FCSTD DOCUMENT  (FreeCAD 0.17R13541 (Git))
Label: L_Wuerth_WE-TPC-3816
License: All rights reserved
LicenseURL: http://en.wikipedia.org/wiki/All_rights_reserved
objects: Sketcher::SketchObject×5, App::Annotation×2, App::DocumentObjectGroup×1
note: 5 computed .brp shape members not serialized (recipe doc carries the construction recipe); baked Part::Feature solids carry a one-line shape summary decoded from their .brp

FEATURE [Sketcher::SketchObject] Sketch004  label="F_Silks_0.12"
  MapMode = 2
  sketch-geometry (2):
    g0: LineSegment StartX=2.01 StartY=0.37 StartZ=0 EndX=2.01 EndY=-0.37 EndZ=0
    g1: LineSegment StartX=-2.01 StartY=-0.37 StartZ=0 EndX=-2.01 EndY=0.37 EndZ=0
  constraints (7):
    c: Vertical(g0)
    c: Vertical(g1)
    c: DistanceX(g1,g0) = 4.02
    c: DistanceY(g0,g0) = 0.74
    c: Equal(g0,g1)
    c: Symmetric(g1,g0,g-2)
    c: Symmetric(g0,g0,g-1)
FEATURE [Sketcher::SketchObject] Sketch  label="F_Fab_0.1"
  MapMode = 2
  Support = -> [Sketch004]
  sketch-geometry (4):
    g0: LineSegment StartX=-1.9 StartY=1.9 StartZ=0 EndX=1.9 EndY=1.9 EndZ=0
    g1: LineSegment StartX=1.9 StartY=1.9 StartZ=0 EndX=1.9 EndY=-1.9 EndZ=0
    g2: LineSegment StartX=1.9 StartY=-1.9 StartZ=0 EndX=-1.9 EndY=-1.9 EndZ=0
    g3: LineSegment StartX=-1.9 StartY=-1.9 StartZ=0 EndX=-1.9 EndY=1.9 EndZ=0
  constraints (11):
    c: Coincident(g0,g1)
    c: Coincident(g1,g2)
    c: Coincident(g2,g3)
    c: Coincident(g3,g0)
    c: Horizontal(g0)
    c: Horizontal(g2)
    c: Vertical(g1)
    c: Vertical(g3)
    c: DistanceY(g1,g1) = 3.8
    c: DistanceX(g2,g2) = 3.8
    c: Symmetric(g1,g0,g-1)
FEATURE [Sketcher::SketchObject] Sketch005  label="F_CrtYd_0.05"
  MapMode = 2
  Support = -> [Sketch]
  sketch-geometry (4):
    g0: LineSegment StartX=-2.4 StartY=2.4 StartZ=0 EndX=2.4 EndY=2.4 EndZ=0
    g1: LineSegment StartX=2.4 StartY=2.4 StartZ=0 EndX=2.4 EndY=-2.4 EndZ=0
    g2: LineSegment StartX=2.4 StartY=-2.4 StartZ=0 EndX=-2.4 EndY=-2.4 EndZ=0
    g3: LineSegment StartX=-2.4 StartY=-2.4 StartZ=0 EndX=-2.4 EndY=2.4 EndZ=0
  constraints (11):
    c: Coincident(g0,g1)
    c: Coincident(g1,g2)
    c: Coincident(g2,g3)
    c: Coincident(g3,g0)
    c: Horizontal(g0)
    c: Horizontal(g2)
    c: Vertical(g1)
    c: Vertical(g3)
    c: DistanceX(g2,g2) = 4.8
    c: DistanceY(g1,g1) = 4.8
    c: Symmetric(g0,g1,g-1)
FEATURE [Sketcher::SketchObject] Sketch006  label="Pads_Poly"
  MapMode = 2
  Support = -> [Sketch005]
  sketch-geometry (8):
    g0: Circle [constr] CenterX=0 CenterY=0 CenterZ=0 NormalX=0 NormalY=0 NormalZ=1 AngleXU=0 Radius=1.3
    g1: Circle CenterX=0 CenterY=1.75 CenterZ=0 NormalX=0 NormalY=0 NormalZ=1 AngleXU=0 Radius=0.35
    g2: ArcOfCircle CenterX=0 CenterY=0 CenterZ=0 NormalX=0 NormalY=0 NormalZ=1 AngleXU=0 Radius=1.3 StartAngle=0.436838 EndAngle=2.70475
    g3: LineSegment StartX=1.17792 StartY=0.55 StartZ=0 EndX=2.15 EndY=0.55 EndZ=0
    g4: LineSegment StartX=2.15 StartY=0.55 StartZ=0 EndX=2.15 EndY=2.15 EndZ=0
    g5: LineSegment StartX=2.15 StartY=2.15 StartZ=0 EndX=-2.15 EndY=2.15 EndZ=0
    g6: LineSegment StartX=-2.15 StartY=2.15 StartZ=0 EndX=-2.15 EndY=0.55 EndZ=0
    g7: LineSegment StartX=-2.15 StartY=0.55 StartZ=0 EndX=-1.17792 EndY=0.55 EndZ=0
  constraints (23):
    c: Coincident(g0,g-1)
    c: Radius(g0) = 1.3
    c: PointOnObject(g1,g-2)
    c: Radius(g1) = 0.35
    c: DistanceY(g-1,g1) = 1.75
    c: PointOnObject(g2,g0)
    c: PointOnObject(g2,g0)
    c: Radius(g2) = 1.3
    c: Coincident(g2,g3)
    c: Horizontal(g3)
    c: Coincident(g3,g4)
    c: Vertical(g4)
    c: Coincident(g4,g5)
    c: Coincident(g5,g6)
    c: Vertical(g6)
    c: Coincident(g6,g7)
    c: Coincident(g7,g2)
    c: Horizontal(g7)
    c: DistanceY(g-1,g6) = 0.55
    c: Horizontal(g2,g2)
    c: DistanceX(g5,g5) = 4.3
    c: DistanceY(g6,g6) = 1.6
    c: Symmetric(g4,g5,g-2)
FEATURE [App::Annotation] Text  label="Ref#_1mm"
  LabelText = REF**
  Position = (0,3,0)
FEATURE [App::Annotation] Text001  label="Value#_1mm"
  LabelText = L_Wuerth_WE-TPC-3816
  Position = (0,-3,0)
FEATURE [Sketcher::SketchObject] Sketch007  label="Pads_Poly001"
  MapMode = 2
  Support = -> [Sketch005]
  sketch-geometry (7):
    g0: Circle CenterX=0 CenterY=-1.75 CenterZ=0 NormalX=0 NormalY=0 NormalZ=1 AngleXU=0 Radius=0.35
    g1: LineSegment StartX=2.15 StartY=-0.55 StartZ=0 EndX=2.15 EndY=-2.15 EndZ=0
    g2: LineSegment StartX=2.15 StartY=-2.15 StartZ=0 EndX=-2.15 EndY=-2.15 EndZ=0
    g3: LineSegment StartX=-2.15 StartY=-2.15 StartZ=0 EndX=-2.15 EndY=-0.55 EndZ=0
    g4: ArcOfCircle CenterX=0 CenterY=0 CenterZ=0 NormalX=0 NormalY=0 NormalZ=1 AngleXU=0 Radius=1.3 StartAngle=3.57843 EndAngle=5.84635
    g5: LineSegment StartX=-2.15 StartY=-0.55 StartZ=0 EndX=-1.17792 EndY=-0.55 EndZ=0
    g6: LineSegment StartX=2.15 StartY=-0.55 StartZ=0 EndX=1.17792 EndY=-0.55 EndZ=0
  constraints (20):
    c: PointOnObject(g0,g-2)
    c: Radius(g0) = 0.35
    c: DistanceY(g0,g-1) = 1.75
    c: DistanceY(g3,g-1) = 0.55
    c: Coincident(g1,g2)
    c: Coincident(g2,g3)
    c: Horizontal(g2)
    c: Vertical(g1)
    c: Vertical(g3)
    c: Distance(g3) = 1.6
    c: Distance(g2) = 4.3
    c: Symmetric(g3,g1,g-2)
    c: Coincident(g4,g-1)
    c: Radius(g4) = 1.3
    c: Coincident(g5,g3)
    c: Coincident(g5,g4)
    c: Horizontal(g5)
    c: Coincident(g6,g1)
    c: Coincident(g6,g4)
    c: Horizontal(g6)
FEATURE [App::DocumentObjectGroup] Group  label="L_Wuerth_WE-TPC-3816"
  Group = -> [Sketch004,Sketch,Sketch005,Sketch006,Text,Text001,Sketch007]
